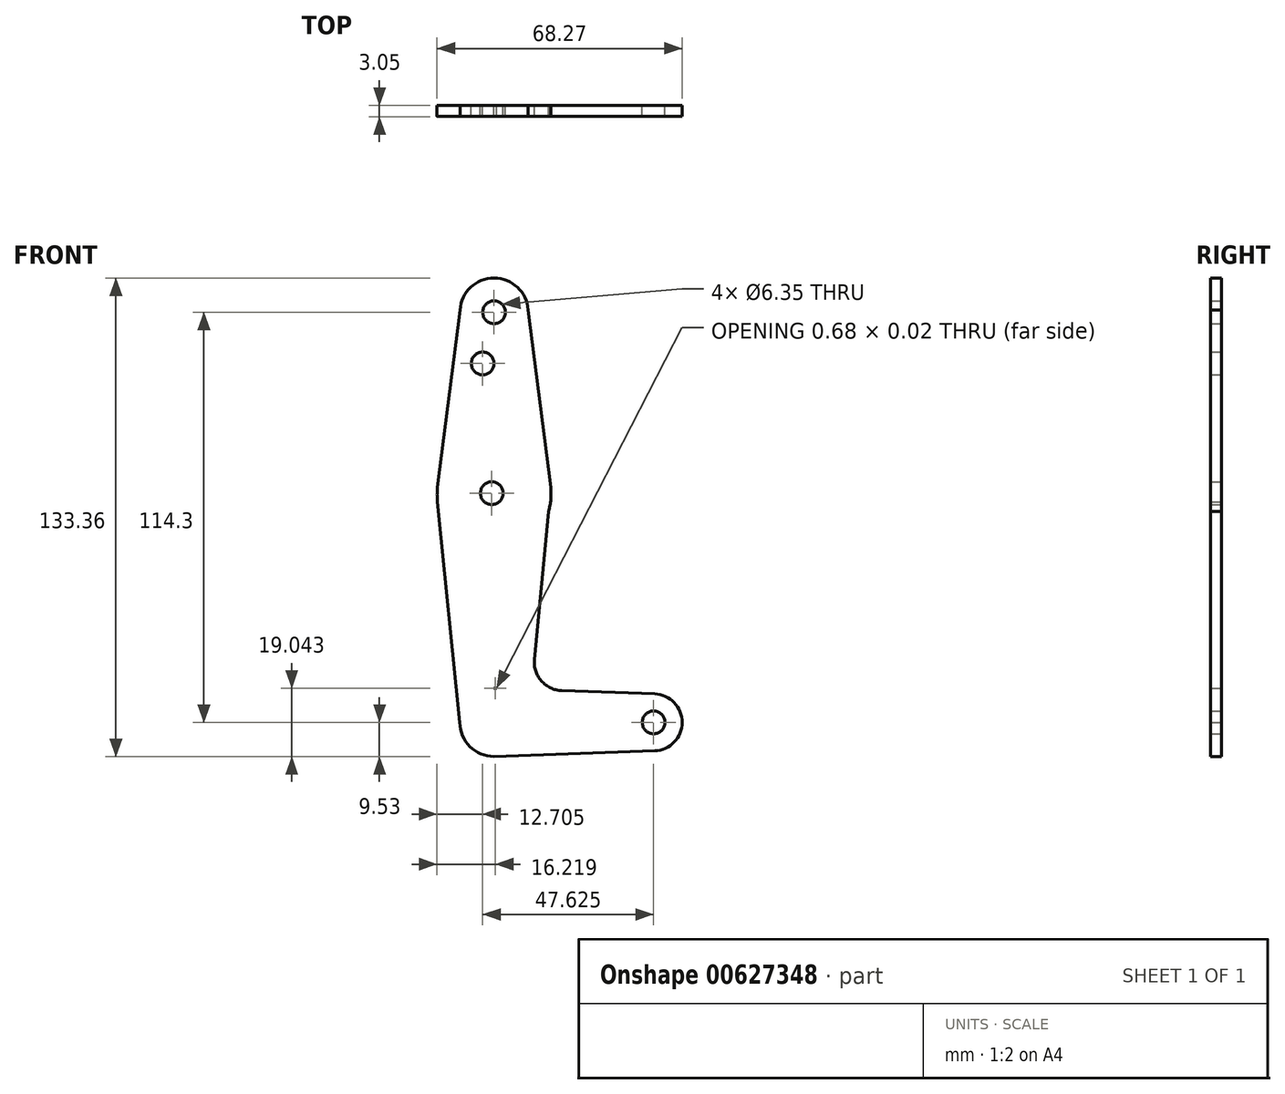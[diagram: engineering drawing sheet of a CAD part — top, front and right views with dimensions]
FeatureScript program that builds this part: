
annotation { "Feature Type Name" : "Feature", "Feature Type Description" : "" }
export const myFeature = defineFeature(function(context is Context, id is Id, definition is map)
    precondition{}
    {
        {
            var Q0;
            Q0=qCreatedBy(makeId("Front.planeOp"),FACE);
            var sketch = newSketch(context, id + "F0", { "sketchPlane" : qUnion([Q0])});
            skLineSegment(sketch, "E0", {"start": v(0, 0) * mm, "end": v(44.45, 0) * mm});
            skCircle(sketch, "E1", {"center": v(0, 63.5) * mm, "radius": 15.88 * mm});
            skCircle(sketch, "E2", {"center": v(0, 0) * mm, "radius": 9.53 * mm});
            skCircle(sketch, "E3", {"center": v(44.45, 0) * mm, "radius": 7.94 * mm});
            skCircle(sketch, "E4", {"center": v(0, 114.3) * mm, "radius": 9.53 * mm});
            skLineSegment(sketch, "E5", {"start": v(0, 0) * mm, "end": v(0, 147.37) * mm, "construction": true});
            skLineSegment(sketch, "E6", {"start": v(9.5, 114.96) * mm, "end": v(15.75, 65.49) * mm});
            skLineSegment(sketch, "E7", {"start": v(-9.5, 114.94) * mm, "end": v(-15.75, 65.49) * mm});
            skLineSegment(sketch, "E8", {"start": v(0, -9.53) * mm, "end": v(44.73, -7.93) * mm});
            skLineSegment(sketch, "E9", {"start": v(0, 9.53) * mm, "end": v(0.68, 9.5) * mm});
            skLineSegment(sketch, "E10.trimOffspring", {"start": v(18.86, 8.85) * mm, "end": v(44.73, 7.93) * mm});
            skLineSegment(sketch, "E11", {"start": v(-9.52, 0) * mm, "end": v(-15.75, 61.51) * mm});
            skLineSegment(sketch, "E12", {"start": v(11.23, 17.55) * mm, "end": v(15.17, 58.83) * mm});
            skPoint(sketch, "E13.visualSharp", {"position": v(10.43, 9.15) * mm});
            skArc(sketch, "E13.filletArc", {"start": v(11.23, 17.55) * mm, "mid": v(13.17, 11.56) * mm, "end": v(18.86, 8.85) * mm});
            skCircle(sketch, "E14", {"center": v(-3.18, 100.03) * mm, "radius": 3.18 * mm});
            skCircle(sketch, "E15", {"center": v(0, 114.3) * mm, "radius": 3.18 * mm});
            skCircle(sketch, "E16", {"center": v(-0.64, 63.87) * mm, "radius": 3.18 * mm});
            skCircle(sketch, "E17", {"center": v(44.45, 0) * mm, "radius": 3.18 * mm});
            skSolve(sketch);
        }
        {
            var Q0;
            {var subQ1=sQuery(id+"F0.wireOp",EDGE,"E6");Q0=makeQuery(id+"F0.imprint","IMPRINT",FACE,{"disambiguationData":[TD([[makeQuery(id+"F0.imprint","IMPRINT",EDGE,{"derivedFrom":subQ1}),-1.0]])]});}
            var Q1;
            {var subQ11=sQuery(id+"F0.wireOp",EDGE,"E10.trimOffspring");Q1=makeQuery(id+"F0.imprint","IMPRINT",FACE,{"disambiguationData":[TD([[makeQuery(id+"F0.imprint","IMPRINT",EDGE,{"derivedFrom":subQ11}),-1.0]])]});}
            var Q2;
            Q2=makeQuery(id+"F0.imprint","IMPRINT",FACE,{"disambiguationData":[TD([[makeQuery(id+"F0.imprint","IMPRINT",EDGE,{"derivedFrom":sQuery(id+"F0.wireOp",EDGE,"E16")}),-1.0]])]});
            var Q3;
            Q3=makeQuery(id+"F0.imprint","IMPRINT",FACE,{"disambiguationData":[TD([[makeQuery(id+"F0.imprint","IMPRINT",EDGE,{"derivedFrom":sQuery(id+"F0.wireOp",EDGE,"E15")}),-1.0]])]});
            var Q4;
            {var subQ4=sQuery(id+"F0.wireOp",EDGE,"E9");Q4=makeQuery(id+"F0.imprint","IMPRINT",FACE,{"disambiguationData":[TD([[makeQuery(id+"F0.imprint","IMPRINT",EDGE,{"derivedFrom":subQ4}),-1.0]])]});}
            var Q5;
            {var subQ0=sQuery(id+"F0.wireOp",EDGE,"E2");var subQ1=sQuery(id+"F0.wireOp",EDGE,"E0");var subQ2=makeQuery(id+"F0.imprint","INTERSECT",VERTEX,{"derivedFrom":[subQ1,subQ0]});Q5=makeQuery(id+"F0.imprint","IMPRINT",FACE,{"disambiguationData":[TD([[makeQuery(id+"F0.imprint","IMPRINT",EDGE,{"disambiguationData":[TD([[subQ2,-1.0]])],"derivedFrom":subQ1}),-1.0]])]});}
            var Q6;
            Q6=makeQuery(id+"F0.imprint","IMPRINT",FACE,{"disambiguationData":[TD([[makeQuery(id+"F0.imprint","IMPRINT",EDGE,{"derivedFrom":sQuery(id+"F0.wireOp",EDGE,"E17")}),-1.0]])]});
            extrude(context, id + "F1", {"entities" : qUnion([Q0, Q1, Q2, Q3, Q4, Q5, Q6]), "depth" : 3.05 * mm, "offsetDistance" : 25.4 * mm});
        }
    });
